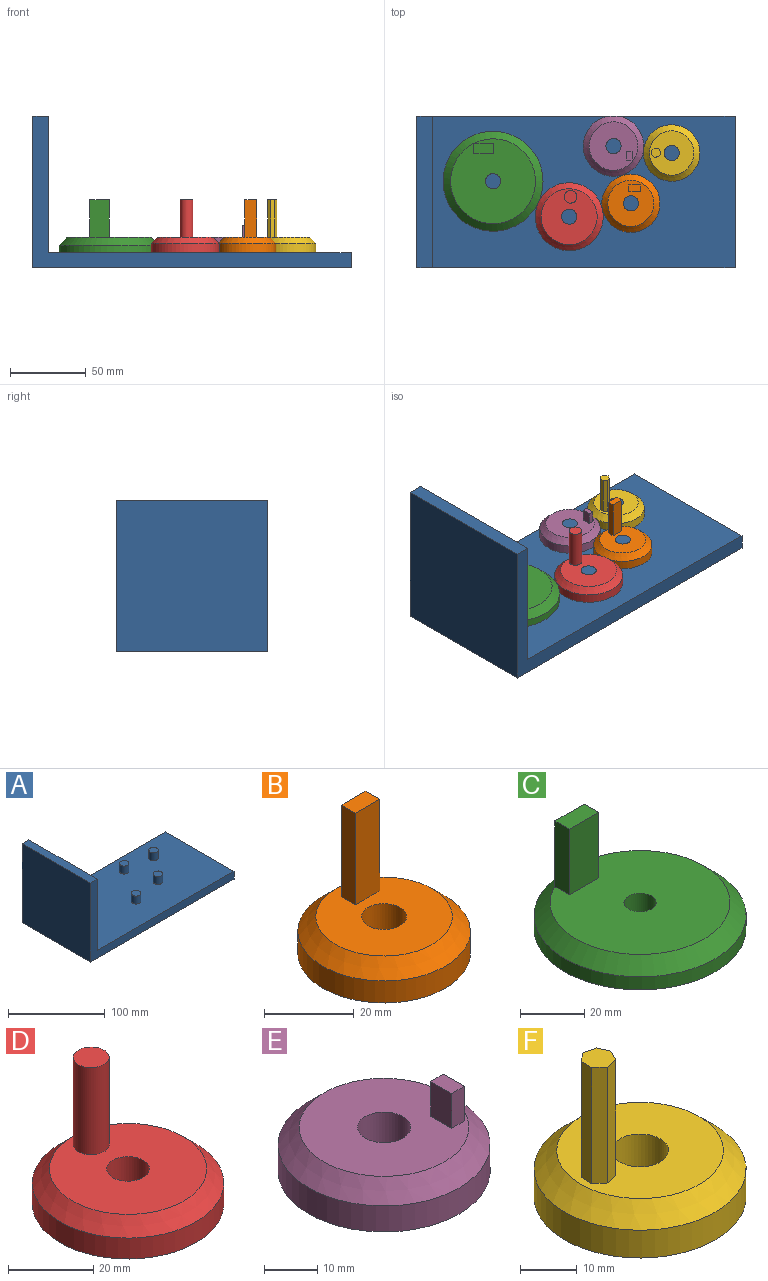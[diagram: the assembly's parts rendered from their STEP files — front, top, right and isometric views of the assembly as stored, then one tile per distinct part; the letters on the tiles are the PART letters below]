
ASSEMBLY  parts=6 mates=5
PART A: 18 faces, bbox 210x100x100 mm
  f0: plane 100x10mm, normal (0,0,1), area 1000mm2, adj f1,f5,f6,f7
  f1: plane 100x100mm, normal (-1,0,0), area 10000mm2, adj f0,f2,f6,f7
  f2: plane 210x100mm, normal (0,0,-1), area 21000mm2, adj f1,f3,f6,f7
  f3: plane 100x10mm, normal (1,0,0), area 1000mm2, adj f2,f4,f6,f7
  f4: plane 200x100mm, normal (0,0,1), area 19607.3mm2, adj f3,f5,f6,f7,f8,f10,f12,f14
  f5: plane 100x90mm, normal (1,0,0), area 9000mm2, adj f0,f4,f6,f7
  f6: plane 210x100mm, normal (0,-1,0), area 3000mm2, adj f0,f1,f2,f3,f4,f5
  f7: plane 210x100mm, normal (0,1,0), area 3000mm2, adj f0,f1,f2,f3,f4,f5
  f8: cylinder r=5mm len=10mm, axis (0,0,-1), area 314.2mm2, adj f4,f9
  f9: plane 10x10mm, normal (0,0,1), area 78.5mm2, adj f8
  f10: cylinder r=5mm len=10mm, axis (0,0,-1), area 314.2mm2, adj f4,f11
  f11: plane 10x10mm, normal (0,0,1), area 78.5mm2, adj f10
  f12: cylinder r=5mm len=10mm, axis (0,0,-1), area 314.2mm2, adj f4,f13
  f13: plane 10x10mm, normal (0,0,1), area 78.5mm2, adj f12
  f14: cylinder r=5mm len=10mm, axis (0,0,-1), area 314.2mm2, adj f4,f15
  f15: plane 10x10mm, normal (0,0,1), area 78.5mm2, adj f14
  f16: cylinder r=5mm len=10mm, axis (0,0,-1), area 314.2mm2, adj f4,f17
  f17: plane 10x10mm, normal (0,0,1), area 78.5mm2, adj f16
PART B: 10 faces, bbox 38.4x38.4x35 mm
  f0: plane 30.44x30.44mm, normal (0,0,1), area 614.6mm2, adj f1,f4,f5,f6,f7,f9
  f1: cylinder r=5mm len=10mm, axis (0,0,-1), area 314.2mm2, adj f0,f3
  f2: cylinder r=19.22mm len=38.44mm, axis (0,0,-1), area 724.5mm2, adj f3,f9
  f3: plane 38.44x38.44mm, normal (0,0,-1), area 1081.8mm2, adj f1,f2
  f4: plane 25x7.77mm, normal (0,1,0), area 194.2mm2, adj f0,f5,f7,f8
  f5: plane 25x4.44mm, normal (-1,0,0), area 111mm2, adj f0,f4,f6,f8
  f6: plane 25x7.77mm, normal (0,-1,0), area 194.2mm2, adj f0,f5,f7,f8
  f7: plane 25x4.44mm, normal (1,0,0), area 111mm2, adj f0,f4,f6,f8
  f8: plane 7.77x4.44mm, normal (0,0,1), area 34.5mm2, adj f4,f5,f6,f7
  f9: cone r=15.22mm half-angle=45deg, axis (0,0,-1), area 612mm2, adj f0,f2
PART C: 10 faces, bbox 66x66x35 mm
  f0: plane 56.01x56.01mm, normal (0,0,1), area 2303.7mm2, adj f1,f4,f5,f6,f7,f9
  f1: cylinder r=5mm len=10mm, axis (0,0,-1), area 314.2mm2, adj f0,f3
  f2: cylinder r=33mm len=66.01mm, axis (0,0,-1), area 1036.9mm2, adj f3,f9
  f3: plane 66.01x66.01mm, normal (0,0,-1), area 3343.6mm2, adj f1,f2
  f4: plane 25x12.89mm, normal (0,-1,0), area 322.2mm2, adj f0,f5,f7,f8
  f5: plane 25x6.34mm, normal (1,0,0), area 158.4mm2, adj f0,f4,f6,f8
  f6: plane 25x12.89mm, normal (0,1,0), area 322.2mm2, adj f0,f5,f7,f8
  f7: plane 25x6.34mm, normal (-1,0,0), area 158.4mm2, adj f0,f4,f6,f8
  f8: plane 12.89x6.34mm, normal (0,0,1), area 81.6mm2, adj f4,f5,f6,f7
  f9: cone r=28mm half-angle=45deg, axis (0,0,-1), area 1355.3mm2, adj f0,f2
PART D: 7 faces, bbox 44.9x44.9x35 mm
  f0: cylinder r=5mm len=10mm, axis (0,0,-1), area 314.2mm2, adj f2,f3
  f1: cylinder r=22.46mm len=44.92mm, axis (0,0,-1), area 846.7mm2, adj f3,f6
  f2: plane 36.92x36.92mm, normal (0,0,1), area 936.1mm2, adj f0,f4,f6
  f3: plane 44.92x44.92mm, normal (0,0,-1), area 1506.1mm2, adj f0,f1
  f4: cylinder r=4.21mm len=25mm, axis (0,0,-1), area 662mm2, adj f2,f5
  f5: plane 8.43x8.43mm, normal (0,0,1), area 55.8mm2, adj f4
  f6: cone r=18.46mm half-angle=45deg, axis (0,0,-1), area 727.2mm2, adj f1,f2
PART E: 11 faces, bbox 40x40x18 mm
  f0: plane 32x32mm, normal (0,0,1), area 706.5mm2, adj f2,f5,f6,f7,f8,f10
  f1: plane 7.79x6.39mm, normal (0,1,0), area 48.7mm2, adj f3,f4,f10
  f2: cylinder r=5mm len=10mm, axis (0,0,-1), area 314.2mm2, adj f0,f4
  f3: cylinder r=20mm len=40mm, axis (0,0,-1), area 707mm2, adj f1,f4,f10
  f4: plane 40x39.62mm, normal (0,0,-1), area 1176.1mm2, adj f1,f2,f3
  f5: plane 8x5.61mm, normal (1,0,0), area 44.9mm2, adj f0,f6,f8,f9
  f6: plane 8x3.42mm, normal (0,1,0), area 27.3mm2, adj f0,f5,f7,f9
  f7: plane 8x5.61mm, normal (-1,0,0), area 44.9mm2, adj f0,f6,f8,f9
  f8: plane 8x3.42mm, normal (0,-1,0), area 27.3mm2, adj f0,f5,f7,f9
  f9: plane 5.61x3.42mm, normal (0,0,1), area 19.2mm2, adj f5,f6,f7,f8
  f10: cone r=16mm half-angle=45deg, axis (0,0,-1), area 637mm2, adj f0,f1,f3
PART F: 13 faces, bbox 37.4x37.4x35 mm
  f0: cylinder r=5mm len=10mm, axis (0,0,-1), area 314.2mm2, adj f2,f3
  f1: cylinder r=18.68mm len=37.36mm, axis (0,0,-1), area 704.2mm2, adj f3,f12
  f2: plane 29.36x29.36mm, normal (0,0,1), area 571.5mm2, adj f0,f4,f5,f6,f7,f8,f9,f10
  f3: plane 37.36x37.36mm, normal (0,0,-1), area 1017.8mm2, adj f0,f1
  f4: plane 25x2.64mm, normal (0.24,0.97,0), area 68.2mm2, adj f2,f5,f10,f11
  f5: plane 25x2.17mm, normal (-0.61,0.8,0), area 68.2mm2, adj f2,f4,f6,f11
  f6: plane 25x2.73mm, normal (-1,0.02,0), area 68.2mm2, adj f2,f5,f7,f11
  f7: plane 25x2.09mm, normal (-0.64,-0.77,0), area 68.2mm2, adj f2,f6,f8,f11
  f8: plane 25x2.67mm, normal (0.2,-0.98,0), area 68.2mm2, adj f2,f7,f9,f11
  f9: plane 25x2.43mm, normal (0.89,-0.45,0), area 68.2mm2, adj f2,f8,f10,f11
  f10: plane 25x2.48mm, normal (0.91,0.41,0), area 68.2mm2, adj f2,f4,f9,f11
  f11: plane 6.12x6mm, normal (0,0,1), area 27mm2, adj f4,f5,f6,f7,f8,f9,f10
  f12: cone r=14.68mm half-angle=45deg, axis (0,0,-1), area 592.9mm2, adj f1,f2
PLACE A t=(-70.12,81.16,-27.21)mm fixed
PLACE B t=(-70.12,81.16,-27.21)mm
PLACE C t=(-70.12,81.16,-27.21)mm
PLACE D t=(-70.12,81.16,-27.21)mm
PLACE E t=(-70.12,81.16,-27.21)mm
PLACE F t=(-70.12,81.16,-27.21)mm
MATE revolute E.f10 <-> A.f10  axis (0,0,-1) through (52.43,61.54,-17.21)mm
MATE revolute B.f1 <-> A.f12  axis (0,0,-1) through (63.9,23.71,-17.21)mm
MATE revolute C.f1 <-> A.f8  axis (0,0,-1) through (-27.13,38.3,-17.21)mm
MATE revolute F.f0 <-> A.f14  axis (0,0,-1) through (90.84,56.96,-17.21)mm
MATE revolute D.f6 <-> A.f16  axis (0,0,-1) through (23.16,14.91,-17.21)mm
